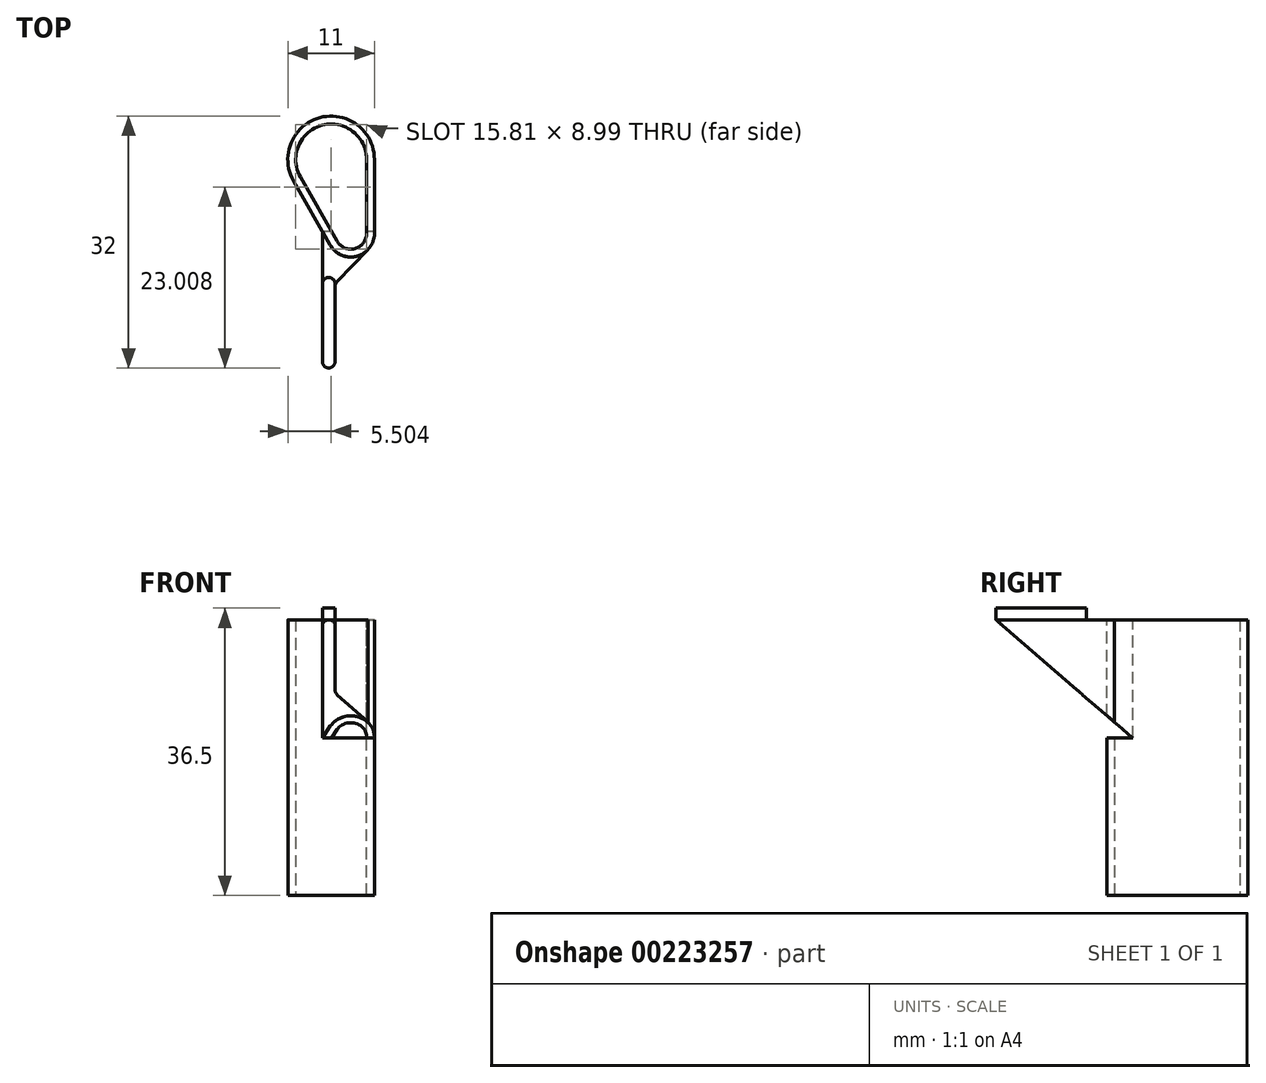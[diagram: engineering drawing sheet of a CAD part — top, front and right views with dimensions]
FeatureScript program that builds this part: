
annotation { "Feature Type Name" : "Feature", "Feature Type Description" : "" }
export const myFeature = defineFeature(function(context is Context, id is Id, definition is map)
    precondition{}
    {
        {
            var Q0;
            Q0=qCreatedBy(makeId("Top.planeOp"),FACE);
            var sketch = newSketch(context, id + "F0", { "sketchPlane" : qUnion([Q0])});
            skCircle(sketch, "E0", {"center": v(0, 0) * mm, "radius": 4.5 * mm});
            skCircle(sketch, "E1", {"center": v(0, 0) * mm, "radius": 5.5 * mm});
            skLineSegment(sketch, "E2", {"start": v(0.5, -15.8) * mm, "end": v(0.5, -25.7) * mm});
            skArc(sketch, "E3", {"start": v(-1.1, -25.7) * mm, "mid": v(-0.3, -26.5) * mm, "end": v(0.5, -25.7) * mm});
            skArc(sketch, "E4", {"start": v(0.5, -15.8) * mm, "mid": v(-0.3, -15) * mm, "end": v(-1.1, -15.8) * mm});
            skLineSegment(sketch, "E5", {"start": v(-1.1, -15.8) * mm, "end": v(-1.1, -25.7) * mm});
            skLineSegment(sketch, "E6", {"start": v(-0.3, -26.5) * mm, "end": v(-10.58, -26.5) * mm, "construction": true});
            skLineSegment(sketch, "E7", {"start": v(-0.3, -15) * mm, "end": v(-9.06, -15) * mm, "construction": true});
            skLineSegment(sketch, "E8", {"start": v(-4.5, 0) * mm, "end": v(-4.5, 7.42) * mm, "construction": true});
            skLineSegment(sketch, "E9", {"start": v(0, 4.5) * mm, "end": v(18.91, 4.5) * mm, "construction": true});
            skSolve(sketch);
        }
        {
            var Q0;
            Q0 = qSketchRegion(id + "F0", true);
            extrude(context, id + "F1", {"entities" : qUnion([Q0]), "depth" : 35 * mm});
        }
        {
            var Q0;
            Q0=makeQuery(id+"F1.opExtrude","CAP_FACE",FACE,{"disambiguationData":[OSD([sQuery(id+"F0.wireOp",EDGE,"E2"),sQuery(id+"F0.wireOp",EDGE,"E3"),sQuery(id+"F0.wireOp",EDGE,"E4"),sQuery(id+"F0.wireOp",EDGE,"E5")])],"isStart":false});
            var sketch = newSketch(context, id + "F2", { "sketchPlane" : qUnion([Q0])});
            skArc(sketch, "E10.0.0", {"start": v(0.5, -15.8) * mm, "mid": v(-0.3, -15) * mm, "end": v(-1.1, -15.8) * mm});
            skLineSegment(sketch, "E10.0.1", {"start": v(-1.1, -15.8) * mm, "end": v(-1.1, -25.7) * mm});
            skArc(sketch, "E10.0.2", {"start": v(-1.1, -25.7) * mm, "mid": v(-0.3, -26.5) * mm, "end": v(0.5, -25.7) * mm});
            skLineSegment(sketch, "E10.0.3", {"start": v(0.5, -25.7) * mm, "end": v(0.5, -15.8) * mm});
            skSolve(sketch);
        }
        {
            var Q0;
            Q0=makeQuery(id+"F2.imprint","IMPRINT",FACE,{"disambiguationData":[TD([[makeQuery(id+"F2.imprint","IMPRINT",EDGE,{"derivedFrom":sQuery(id+"F2.wireOp",EDGE,"E10.0.0")}),1.0]])]});
            extrude(context, id + "F3", {"entities" : qUnion([Q0]), "operationType" : NewBodyOperationType.ADD, "depth" : 1.5 * mm});
        }
        {
            var Q0;
            Q0=makeQuery(id+"F1.opExtrude","CAP_FACE",FACE,{"disambiguationData":[OSD([sQuery(id+"F0.wireOp",EDGE,"E2"),sQuery(id+"F0.wireOp",EDGE,"E3"),sQuery(id+"F0.wireOp",EDGE,"E4"),sQuery(id+"F0.wireOp",EDGE,"E5")])],"isStart":true});
            var sketch = newSketch(context, id + "F4", { "sketchPlane" : qUnion([Q0])});
            skArc(sketch, "E11.0.0", {"start": v(-1.1, 15.8) * mm, "mid": v(-0.3, 15) * mm, "end": v(0.5, 15.8) * mm});
            skLineSegment(sketch, "E11.0.1", {"start": v(0.5, 15.8) * mm, "end": v(0.5, 25.7) * mm});
            skArc(sketch, "E11.0.2", {"start": v(0.5, 25.7) * mm, "mid": v(-0.3, 26.5) * mm, "end": v(-1.1, 25.7) * mm});
            skLineSegment(sketch, "E11.0.3", {"start": v(-1.1, 25.7) * mm, "end": v(-1.1, 15.8) * mm});
            skSolve(sketch);
        }
        {
            var Q0;
            Q0=makeQuery(id+"F4.imprint","IMPRINT",FACE,{"disambiguationData":[TD([[makeQuery(id+"F4.imprint","IMPRINT",EDGE,{"derivedFrom":sQuery(id+"F4.wireOp",EDGE,"E11.0.0")}),-1.0]])]});
            extrude(context, id + "F5", {"entities" : qUnion([Q0]), "operationType" : NewBodyOperationType.REMOVE, "oppositeDirection" : true, "depth" : 35 * mm});
        }
        {
            var Q0;
            Q0=makeQuery(id+"F1.opExtrude","CAP_FACE",FACE,{"disambiguationData":[OSD([sQuery(id+"F0.wireOp",EDGE,"E0"),sQuery(id+"F0.wireOp",EDGE,"E1")])],"isStart":false});
            var sketch = newSketch(context, id + "F6", { "sketchPlane" : qUnion([Q0])});
            skLineSegment(sketch, "E12.0.0", {"start": v(0.5, -25.7) * mm, "end": v(0.5, -15.8) * mm});
            skArc(sketch, "E12.0.1", {"start": v(0.5, -15.8) * mm, "mid": v(-0.3, -15) * mm, "end": v(-1.1, -15.8) * mm});
            skLineSegment(sketch, "E12.0.2", {"start": v(-1.1, -15.8) * mm, "end": v(-1.1, -25.7) * mm});
            skArc(sketch, "E12.0.3", {"start": v(-1.1, -25.7) * mm, "mid": v(-0.3, -26.5) * mm, "end": v(0.5, -25.7) * mm});
            skLineSegment(sketch, "E13", {"start": v(-0.3, -15) * mm, "end": v(-4.82, -15) * mm});
            skLineSegment(sketch, "E14", {"start": v(0.5, 0.6) * mm, "end": v(0.5, -9.4) * mm});
            skLineSegment(sketch, "E15.0", {"start": v(4.5, 0.6) * mm, "end": v(4.5, -9.4) * mm});
            skArc(sketch, "E16", {"start": v(4.5, 0.6) * mm, "mid": v(2.5, 2.6) * mm, "end": v(0.5, 0.6) * mm});
            skArc(sketch, "E17", {"start": v(0.5, -9.4) * mm, "mid": v(2.5, -11.4) * mm, "end": v(4.5, -9.4) * mm});
            skLineSegment(sketch, "E18.0", {"start": v(5.5, 0.6) * mm, "end": v(5.5, -9.4) * mm});
            skArc(sketch, "E18.1", {"start": v(5.5, 0.6) * mm, "mid": v(2.5, 3.6) * mm, "end": v(-0.5, 0.6) * mm});
            skLineSegment(sketch, "E18.2", {"start": v(-0.5, 0.6) * mm, "end": v(-0.5, -9.4) * mm});
            skArc(sketch, "E18.3", {"start": v(-0.5, -9.4) * mm, "mid": v(2.5, -12.4) * mm, "end": v(5.5, -9.4) * mm});
            skLineSegment(sketch, "E19", {"start": v(-0.1, -10.9) * mm, "end": v(-4.77, -2.73) * mm});
            skLineSegment(sketch, "E20", {"start": v(-3.9, -2.24) * mm, "end": v(0.76, -10.4) * mm});
            skSolve(sketch);
        }
        {
            var Q0;
            {var subQ5=sQuery(id+"F6.wireOp",EDGE,"E19");Q0=makeQuery(id+"F6.imprint","IMPRINT",FACE,{"disambiguationData":[TD([[makeQuery(id+"F6.imprint","IMPRINT",EDGE,{"derivedFrom":subQ5}),-1.0]])]});}
            var Q1;
            {var subQ9=sQuery(id+"F6.wireOp",EDGE,"E17");var subQ10=sQuery(id+"F6.wireOp",EDGE,"E15.0");var subQ11=makeQuery(id+"F6.imprint","INTERSECT",VERTEX,{"derivedFrom":[subQ10,subQ9]});Q1=makeQuery(id+"F6.imprint","IMPRINT",FACE,{"disambiguationData":[TD([[makeQuery(id+"F6.imprint","IMPRINT",EDGE,{"disambiguationData":[TD([[subQ11,1.0]])],"derivedFrom":subQ10}),1.0]])]});}
            extrude(context, id + "F7", {"entities" : qUnion([Q0, Q1]), "operationType" : NewBodyOperationType.ADD, "oppositeDirection" : true, "depth" : 35 * mm});
        }
        {
            var Q0;
            {var subQ0=sQuery(id+"F0.wireOp",EDGE,"E1");Q0=makeQuery(id+"F7.boolean.opBoolean","MERGE",FACE,{"derivedFrom":[makeQuery(id+"F1.opExtrude","CAP_FACE",FACE,{"disambiguationData":[OSD([sQuery(id+"F0.wireOp",EDGE,"E0"),subQ0])],"isStart":false}),makeQuery(id+"F7.opExtrude","CAP_FACE",FACE,{"disambiguationData":[OSD([subQ0,sQuery(id+"F6.wireOp",EDGE,"E15.0"),sQuery(id+"F6.wireOp",EDGE,"E17"),sQuery(id+"F6.wireOp",EDGE,"E18.0"),sQuery(id+"F6.wireOp",EDGE,"E18.3"),sQuery(id+"F6.wireOp",EDGE,"E19"),sQuery(id+"F6.wireOp",EDGE,"E20")])],"isStart":true})]});}
            var sketch = newSketch(context, id + "F8", { "sketchPlane" : qUnion([Q0])});
            skLineSegment(sketch, "E21.0.0", {"start": v(5.5, -9.4) * mm, "end": v(5.5, 0) * mm});
            skArc(sketch, "E21.0.1", {"start": v(5.5, 0) * mm, "mid": v(-1.41, 5.32) * mm, "end": v(-4.77, -2.73) * mm});
            skLineSegment(sketch, "E21.0.2", {"start": v(-4.77, -2.73) * mm, "end": v(-0.1, -10.9) * mm});
            skArc(sketch, "E21.0.3", {"start": v(-0.1, -10.9) * mm, "mid": v(3.27, -12.3) * mm, "end": v(5.5, -9.4) * mm});
            skLineSegment(sketch, "E22", {"start": v(-2.33, -4.98) * mm, "end": v(-3.9, -2.24) * mm});
            skLineSegment(sketch, "E23", {"start": v(4.5, -3.16) * mm, "end": v(4.5, 0) * mm});
            skSolve(sketch);
        }
        {
            var Q0;
            {var subQ0=sQuery(id+"F8.wireOp",EDGE,"E22");Q0=makeQuery(id+"F8.imprint","IMPRINT",FACE,{"disambiguationData":[TD([[makeQuery(id+"F8.imprint","IMPRINT",EDGE,{"derivedFrom":subQ0}),-1.0]])]});}
            extrude(context, id + "F9", {"entities" : qUnion([Q0]), "operationType" : NewBodyOperationType.REMOVE, "endBound" : BoundingType.THROUGH_ALL, "oppositeDirection" : true, "depth" : 25 * mm});
        }
        {
            var Q0;
            {var subQ0=sQuery(id+"F0.wireOp",EDGE,"E1");Q0=makeQuery(id+"F7.boolean.opBoolean","MERGE",FACE,{"derivedFrom":[makeQuery(id+"F1.opExtrude","CAP_FACE",FACE,{"disambiguationData":[OSD([sQuery(id+"F0.wireOp",EDGE,"E0"),subQ0])],"isStart":false}),makeQuery(id+"F7.opExtrude","CAP_FACE",FACE,{"disambiguationData":[OSD([subQ0,sQuery(id+"F6.wireOp",EDGE,"E15.0"),sQuery(id+"F6.wireOp",EDGE,"E17"),sQuery(id+"F6.wireOp",EDGE,"E18.0"),sQuery(id+"F6.wireOp",EDGE,"E18.3"),sQuery(id+"F6.wireOp",EDGE,"E19"),sQuery(id+"F6.wireOp",EDGE,"E20")])],"isStart":true})]});}
            var sketch = newSketch(context, id + "F10", { "sketchPlane" : qUnion([Q0])});
            skLineSegment(sketch, "E24.0.0", {"start": v(0.5, -25.7) * mm, "end": v(0.5, -15.8) * mm});
            skArc(sketch, "E24.0.1", {"start": v(0.5, -15.8) * mm, "mid": v(-0.3, -15) * mm, "end": v(-1.1, -15.8) * mm});
            skLineSegment(sketch, "E24.0.2", {"start": v(-1.1, -15.8) * mm, "end": v(-1.1, -25.7) * mm});
            skArc(sketch, "E24.0.3", {"start": v(-1.1, -25.7) * mm, "mid": v(-0.3, -26.5) * mm, "end": v(0.5, -25.7) * mm});
            skLineSegment(sketch, "E25", {"start": v(-1.1, -15.8) * mm, "end": v(-1.1, -9.15) * mm});
            skLineSegment(sketch, "E26", {"start": v(0.5, -15.8) * mm, "end": v(4.66, -11.48) * mm});
            skSolve(sketch);
        }
        {
            var Q0;
            Q0=makeQuery(id+"F10.imprint","IMPRINT",FACE,{"disambiguationData":[TD([[makeQuery(id+"F10.imprint","IMPRINT",EDGE,{"derivedFrom":sQuery(id+"F10.wireOp",EDGE,"E24.0.1")}),-1.0]])]});
            var Q1;
            Q1=makeQuery(id+"F10.imprint","IMPRINT",FACE,{"disambiguationData":[TD([[makeQuery(id+"F10.imprint","IMPRINT",EDGE,{"derivedFrom":sQuery(id+"F10.wireOp",EDGE,"E24.0.0")}),1.0]])]});
            extrude(context, id + "F11", {"entities" : qUnion([Q0, Q1]), "oppositeDirection" : true, "depth" : 15 * mm});
        }
        {
            var Q0;
            Q0=makeQuery(id+"F11.opExtrude","SWEPT_FACE",FACE,{"disambiguationData":[OSD([sQuery(id+"F10.wireOp",EDGE,"E24.0.2"),sQuery(id+"F10.wireOp",EDGE,"E25")])]});
            var sketch = newSketch(context, id + "F12", { "sketchPlane" : qUnion([Q0])});
            skLineSegment(sketch, "E27.0.0", {"start": v(15.8, 36.5) * mm, "end": v(15.8, 35) * mm});
            skLineSegment(sketch, "E27.0.1", {"start": v(15.8, 35) * mm, "end": v(15, 35) * mm});
            skLineSegment(sketch, "E27.0.2", {"start": v(15.8, 35) * mm, "end": v(15.8, 36.5) * mm});
            skLineSegment(sketch, "E27.0.3", {"start": v(15.8, 36.5) * mm, "end": v(15, 36.5) * mm});
            skLineSegment(sketch, "E28.0.0", {"start": v(25.7, 36.5) * mm, "end": v(25.7, 35) * mm});
            skLineSegment(sketch, "E28.0.1", {"start": v(25.7, 35) * mm, "end": v(26.5, 35) * mm});
            skLineSegment(sketch, "E28.0.2", {"start": v(25.7, 35) * mm, "end": v(25.7, 36.5) * mm});
            skLineSegment(sketch, "E28.0.3", {"start": v(25.7, 36.5) * mm, "end": v(26.5, 36.5) * mm});
            skLineSegment(sketch, "E29", {"start": v(15, 35) * mm, "end": v(15, 20) * mm});
            skLineSegment(sketch, "E30", {"start": v(25.7, 35) * mm, "end": v(15.8, 35) * mm});
            skLineSegment(sketch, "E31.0.1", {"start": v(25.7, 35) * mm, "end": v(25.7, 20) * mm});
            skLineSegment(sketch, "E31.0.2", {"start": v(25.7, 20) * mm, "end": v(26.5, 20) * mm});
            skLineSegment(sketch, "E31.0.3", {"start": v(25.7, 20) * mm, "end": v(25.7, 35) * mm});
            skLineSegment(sketch, "E32", {"start": v(26.5, 35) * mm, "end": v(26.5, 20) * mm});
            skLineSegment(sketch, "E33", {"start": v(26.5, 35) * mm, "end": v(9.15, 20) * mm});
            skSolve(sketch);
        }
        {
            var Q0;
            {var subQ0=sQuery(id+"F12.wireOp",EDGE,"E29");var subQ4=sQuery(id+"F12.wireOp",EDGE,"E33");var subQ5=makeQuery(id+"F12.imprint","INTERSECT",VERTEX,{"derivedFrom":[subQ0,subQ4]});Q0=makeQuery(id+"F12.imprint","IMPRINT",FACE,{"disambiguationData":[TD([[makeQuery(id+"F12.imprint","IMPRINT",EDGE,{"disambiguationData":[TD([[subQ5,-1.0]])],"derivedFrom":subQ0}),-1.0]])]});}
            var Q1;
            {var subQ0=sQuery(id+"F12.wireOp",EDGE,"E29");var subQ3=sQuery(id+"F12.wireOp",EDGE,"E33");var subQ4=makeQuery(id+"F12.imprint","INTERSECT",VERTEX,{"derivedFrom":[subQ0,subQ3]});Q1=makeQuery(id+"F12.imprint","IMPRINT",FACE,{"disambiguationData":[TD([[makeQuery(id+"F12.imprint","IMPRINT",EDGE,{"disambiguationData":[TD([[subQ4,1.0]])],"derivedFrom":subQ3}),1.0]])]});}
            var Q2;
            {var subQ0=sQuery(id+"F12.wireOp",EDGE,"E31.0.2");Q2=makeQuery(id+"F12.imprint","IMPRINT",FACE,{"disambiguationData":[TD([[makeQuery(id+"F12.imprint","IMPRINT",EDGE,{"derivedFrom":subQ0}),1.0]])]});}
            extrude(context, id + "F13", {"entities" : qUnion([Q0, Q1, Q2]), "operationType" : NewBodyOperationType.REMOVE, "oppositeDirection" : true, "depth" : 25 * mm});
        }
        {
            var Q0;
            Q0=makeQuery(id+"F11.opExtrude","SWEPT_EDGE",EDGE,{"disambiguationData":[OSD([sQuery(id+"F10.wireOp",EDGE,"E24.0.0"),sQuery(id+"F10.wireOp",EDGE,"E24.0.1"),sQuery(id+"F10.wireOp",EDGE,"E26")])]});
            fillet(context, id + "F14", {"entities" : qUnion([Q0]), "radius" : 1 * mm, "tangentPropagation" : true, "allowEdgeOverflow" : false});
        }
    });
